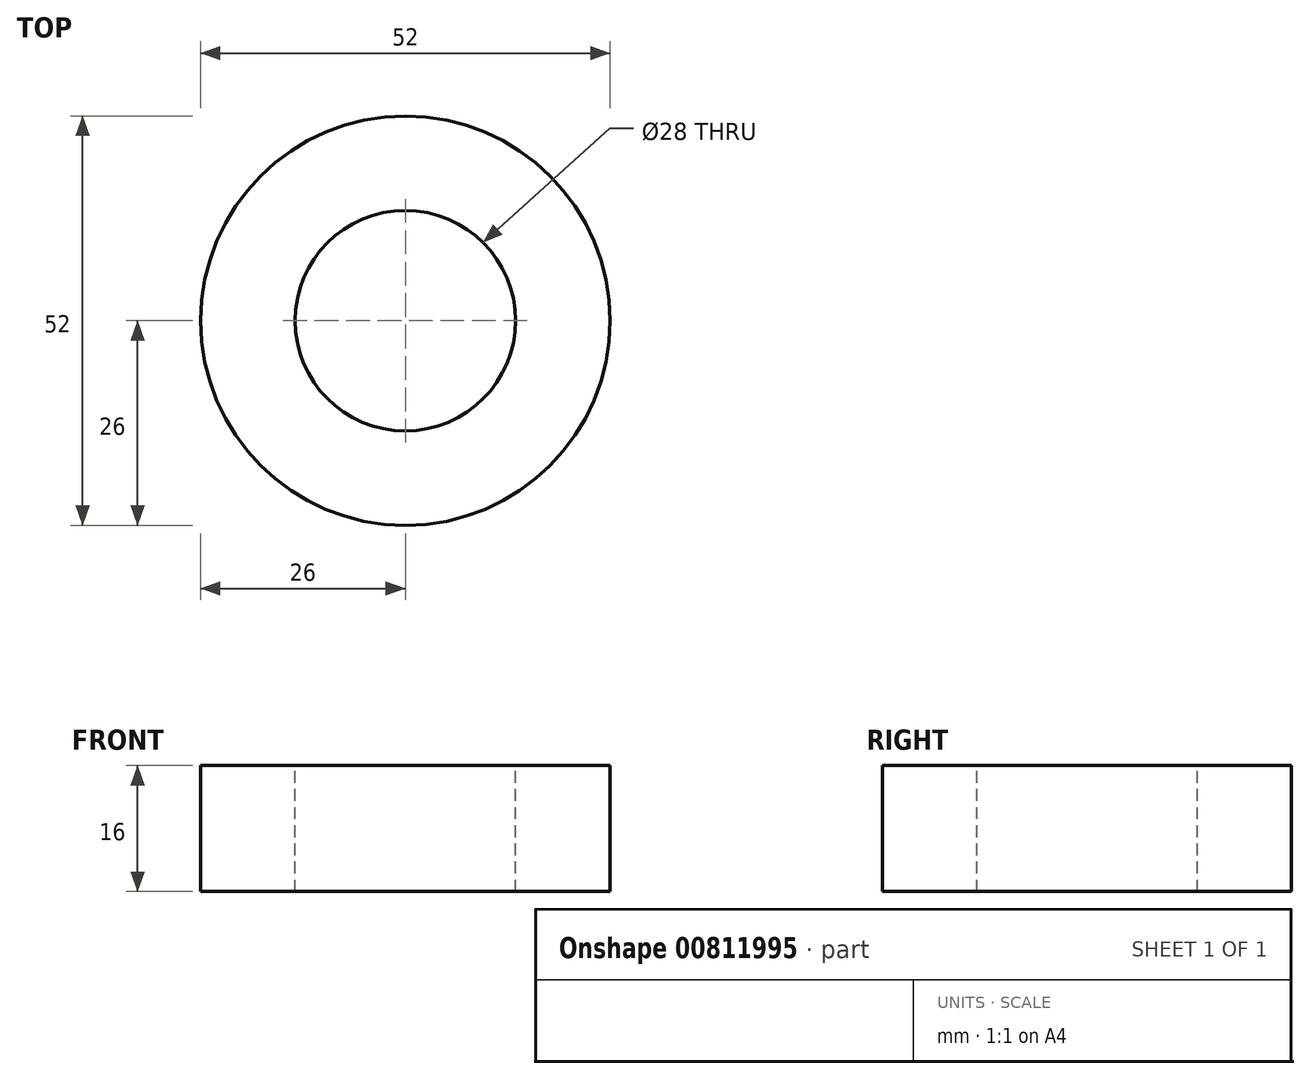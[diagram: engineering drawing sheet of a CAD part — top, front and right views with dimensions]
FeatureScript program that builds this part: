
annotation { "Feature Type Name" : "Feature", "Feature Type Description" : "" }
export const myFeature = defineFeature(function(context is Context, id is Id, definition is map)
    precondition{}
    {
        {
            var Q0;
            Q0=qCreatedBy(makeId("Front.planeOp"),FACE);
            var sketch = newSketch(context, id + "F0", { "sketchPlane" : qUnion([Q0])});
            skLineSegment(sketch, "E0", {"start": v(0, 73.26) * mm, "end": v(0, -76.51) * mm, "construction": true});
            skLineSegment(sketch, "E1", {"start": v(-14, 5.9) * mm, "end": v(-14, -10.1) * mm});
            skLineSegment(sketch, "E2", {"start": v(-26, -10.1) * mm, "end": v(-14, -10.1) * mm});
            skLineSegment(sketch, "E3", {"start": v(-26, -10.1) * mm, "end": v(-26, 5.9) * mm});
            skLineSegment(sketch, "E4", {"start": v(-14, 5.9) * mm, "end": v(-26, 5.9) * mm});
            skSolve(sketch);
        }
        {
            var Q0;
            Q0 = qSketchRegion(id + "F0", true);
            var Q1;
            Q1=sQuery(id+"F0.wireOp",EDGE,"E0");
            revolve(context, id + "F1", {"surfaceOperationType" : NewSurfaceOperationType.NEW, "entities" : qUnion([Q0]), "axis" : qUnion([Q1]), "revolveType" : RevolveType.FULL});
        }
    });
